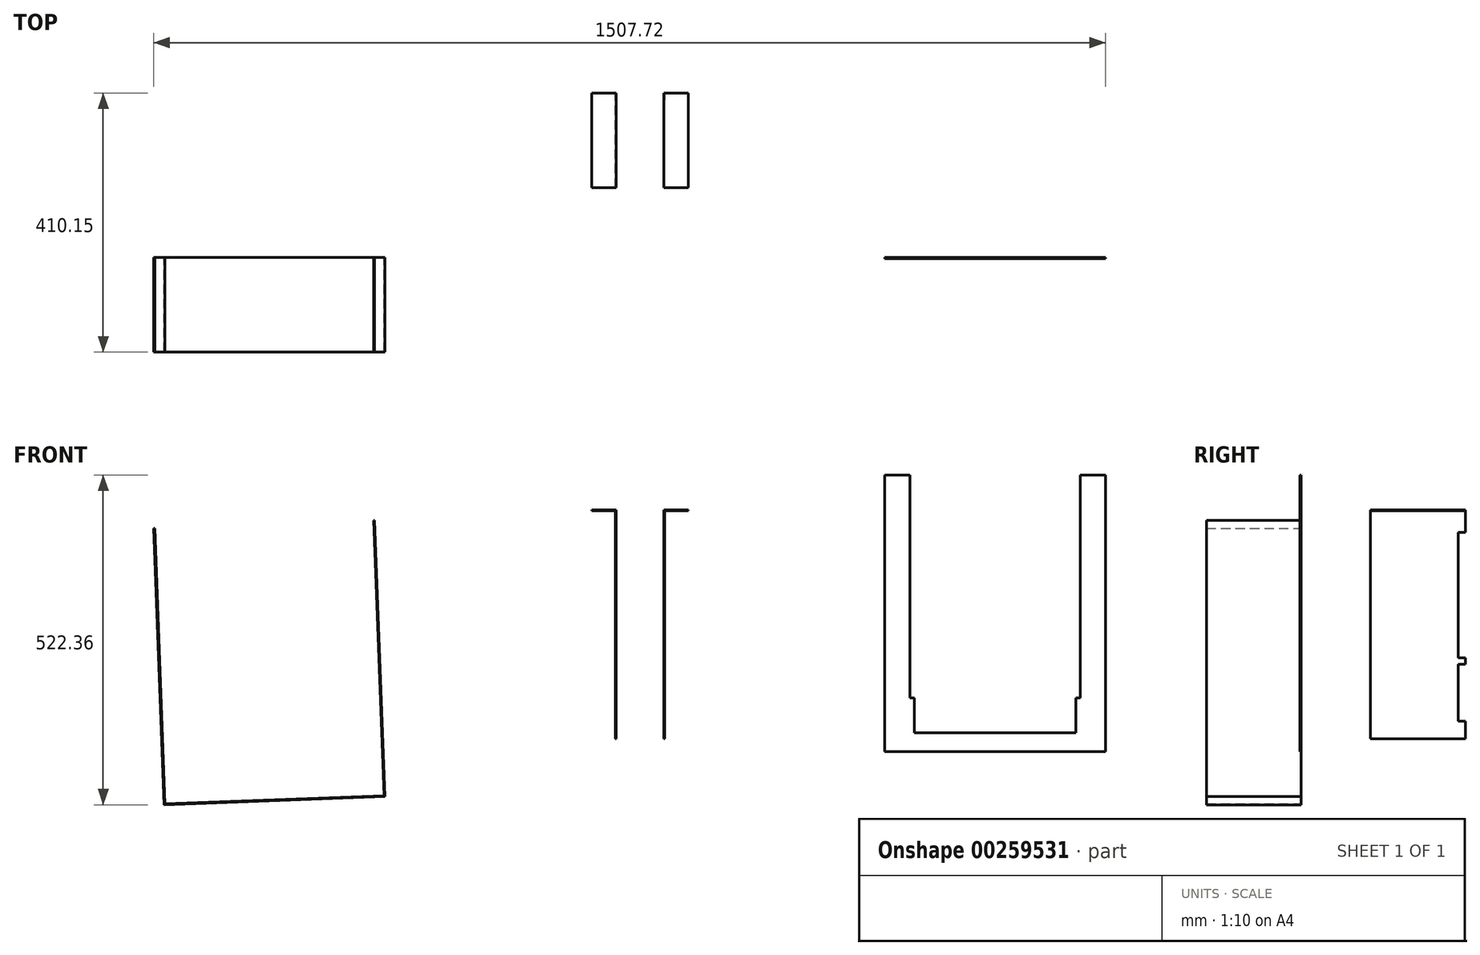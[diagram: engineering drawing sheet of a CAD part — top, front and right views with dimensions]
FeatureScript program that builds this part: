
annotation { "Feature Type Name" : "Feature", "Feature Type Description" : "" }
export const myFeature = defineFeature(function(context is Context, id is Id, definition is map)
    precondition{}
    {
        {
            var Q0;
            Q0=qCreatedBy(makeId("Front.planeOp"),FACE);
            var sketch = newSketch(context, id + "F0", { "sketchPlane" : qUnion([Q0])});
            skLineSegment(sketch, "E0", {"start": v(-308.3, 139.8) * mm, "end": v(-291.9, -297.9) * mm});
            skLineSegment(sketch, "E1", {"start": v(-291.9, -297.9) * mm, "end": v(-641.65, -311) * mm});
            skLineSegment(sketch, "E2", {"start": v(-641.65, -311) * mm, "end": v(-658.05, 126.7) * mm});
            skLineSegment(sketch, "E3", {"start": v(-658.05, 126.7) * mm, "end": v(-656.55, 126.75) * mm});
            skLineSegment(sketch, "E4", {"start": v(-656.55, 126.75) * mm, "end": v(-640.21, -309.44) * mm});
            skLineSegment(sketch, "E5", {"start": v(-640.21, -309.44) * mm, "end": v(-293.46, -296.45) * mm});
            skLineSegment(sketch, "E6", {"start": v(-293.46, -296.45) * mm, "end": v(-309.8, 139.74) * mm});
            skLineSegment(sketch, "E7", {"start": v(-309.8, 139.74) * mm, "end": v(-308.3, 139.8) * mm});
            skSolve(sketch);
        }
        {
            var Q0;
            Q0 = qSketchRegion(id + "F0", true);
            extrude(context, id + "F1", {"entities" : qUnion([Q0]), "depth" : 150 * mm});
        }
        {
            var Q0;
            Q0=qCreatedBy(makeId("Right.planeOp"),FACE);
            var sketch = newSketch(context, id + "F2", { "sketchPlane" : qUnion([Q0])});
            skLineSegment(sketch, "E8", {"start": v(148.65, 156.28) * mm, "end": v(110.15, 156.28) * mm});
            skLineSegment(sketch, "E9", {"start": v(110.15, 156.28) * mm, "end": v(110.15, -206.72) * mm});
            skLineSegment(sketch, "E10", {"start": v(110.15, -206.72) * mm, "end": v(111.65, -206.72) * mm});
            skLineSegment(sketch, "E11", {"start": v(111.65, -206.72) * mm, "end": v(111.65, 154.78) * mm});
            skLineSegment(sketch, "E12", {"start": v(111.65, 154.78) * mm, "end": v(148.65, 154.78) * mm});
            skLineSegment(sketch, "E13", {"start": v(148.65, 154.78) * mm, "end": v(148.65, 156.28) * mm});
            skSolve(sketch);
        }
        {
            var Q0;
            Q0=makeQuery(id+"F2.imprint","IMPRINT",FACE,{"disambiguationData":[TD([[makeQuery(id+"F2.imprint","IMPRINT",EDGE,{"derivedFrom":sQuery(id+"F2.wireOp",EDGE,"E8")}),1.0]])]});
            extrude(context, id + "F3", {"entities" : qUnion([Q0]), "depth" : 150 * mm});
        }
        {
            var Q0;
            Q0=makeQuery(id+"F3.opExtrude","SWEPT_FACE",FACE,{"disambiguationData":[OSD([sQuery(id+"F2.wireOp",EDGE,"E11")])]});
            var sketch = newSketch(context, id + "F4", { "sketchPlane" : qUnion([Q0])});
            skLineSegment(sketch, "E14", {"start": v(0, 120.28) * mm, "end": v(-11, 120.28) * mm});
            skLineSegment(sketch, "E15", {"start": v(-11, 120.28) * mm, "end": v(-11, -78.2) * mm});
            skLineSegment(sketch, "E16", {"start": v(-11, -78.2) * mm, "end": v(0, -78.2) * mm});
            skLineSegment(sketch, "E17", {"start": v(0, -88.2) * mm, "end": v(-11, -88.2) * mm});
            skLineSegment(sketch, "E18", {"start": v(-11, -88.2) * mm, "end": v(-11, -178.72) * mm});
            skLineSegment(sketch, "E19", {"start": v(-11, -178.72) * mm, "end": v(0, -178.72) * mm});
            skSolve(sketch);
        }
        {
            var Q0;
            {var subQ0=sQuery(id+"F4.wireOp",EDGE,"E14");Q0=makeQuery(id+"F4.imprint","IMPRINT",FACE,{"disambiguationData":[TD([[makeQuery(id+"F4.imprint","IMPRINT",EDGE,{"derivedFrom":subQ0}),1.0]])]});}
            var Q1;
            {var subQ0=sQuery(id+"F4.wireOp",EDGE,"E17");Q1=makeQuery(id+"F4.imprint","IMPRINT",FACE,{"disambiguationData":[TD([[makeQuery(id+"F4.imprint","IMPRINT",EDGE,{"derivedFrom":subQ0}),1.0]])]});}
            extrude(context, id + "F5", {"entities" : qUnion([Q0, Q1]), "operationType" : NewBodyOperationType.REMOVE, "oppositeDirection" : true, "depth" : 1.5 * mm});
        }
        {
            var Q0;
            Q0=makeQuery(id+"F3.opExtrude","SWEPT_BODY",BODY,{"disambiguationData":[OSD([sQuery(id+"F2.wireOp",EDGE,"E8"),sQuery(id+"F2.wireOp",EDGE,"E9"),sQuery(id+"F2.wireOp",EDGE,"E10"),sQuery(id+"F2.wireOp",EDGE,"E11"),sQuery(id+"F2.wireOp",EDGE,"E12"),sQuery(id+"F2.wireOp",EDGE,"E13")])]});
            var Q1;
            Q1=makeQuery(id+"F3.opExtrude","CAP_EDGE",EDGE,{"disambiguationData":[OSD([sQuery(id+"F2.wireOp",EDGE,"E9")])],"isStart":false});
            transform(context, id + "F6", {"entities" : qUnion([Q0]), "transformType" : TransformType.ROTATION, "transformAxis" : qUnion([Q1]), "angle" : 90 * degree, "makeCopy" : false});
        }
        {
            var Q0;
            Q0=makeQuery(id+"F3.opExtrude","SWEPT_BODY",BODY,{"disambiguationData":[OSD([sQuery(id+"F2.wireOp",EDGE,"E8"),sQuery(id+"F2.wireOp",EDGE,"E9"),sQuery(id+"F2.wireOp",EDGE,"E10"),sQuery(id+"F2.wireOp",EDGE,"E11"),sQuery(id+"F2.wireOp",EDGE,"E12"),sQuery(id+"F2.wireOp",EDGE,"E13")])]});
            var Q1;
            Q1=makeQuery(id+"F3.opExtrude","CAP_EDGE",EDGE,{"disambiguationData":[OSD([sQuery(id+"F2.wireOp",EDGE,"E12")])],"isStart":true});
            transform(context, id + "F7", {"entities" : qUnion([Q0]), "transformType" : TransformType.TRANSLATION_ENTITY, "oppositeDirectionEntity" : true, "transformLine" : qUnion([Q1]), "makeCopy" : true});
        }
        {
            var Q0;
            Q0=makeQuery(id+"F7.opPattern","COPY",BODY,{"derivedFrom":makeQuery(id+"F3.opExtrude","SWEPT_BODY",BODY,{"disambiguationData":[OSD([sQuery(id+"F2.wireOp",EDGE,"E8"),sQuery(id+"F2.wireOp",EDGE,"E9"),sQuery(id+"F2.wireOp",EDGE,"E10"),sQuery(id+"F2.wireOp",EDGE,"E11"),sQuery(id+"F2.wireOp",EDGE,"E12"),sQuery(id+"F2.wireOp",EDGE,"E13")])]}),"instanceName":"1"});
            var Q1;
            Q1=makeQuery(id+"F7.opPattern","COPY",EDGE,{"derivedFrom":makeQuery(id+"F3.opExtrude","CAP_EDGE",EDGE,{"disambiguationData":[OSD([sQuery(id+"F2.wireOp",EDGE,"E8")])],"isStart":true}),"instanceName":"1"});
            transform(context, id + "F8", {"entities" : qUnion([Q0]), "transformType" : TransformType.TRANSLATION_ENTITY, "oppositeDirectionEntity" : false, "transformLine" : qUnion([Q1]), "makeCopy" : false});
        }
        {
            var Q0;
            Q0=qCreatedBy(makeId("Front.planeOp"),FACE);
            var sketch = newSketch(context, id + "F9", { "sketchPlane" : qUnion([Q0])});
            skLineSegment(sketch, "E20", {"start": v(849.67, 211.36) * mm, "end": v(849.67, -226.64) * mm});
            skLineSegment(sketch, "E21", {"start": v(849.67, -226.64) * mm, "end": v(499.67, -226.64) * mm});
            skLineSegment(sketch, "E22", {"start": v(499.67, -226.64) * mm, "end": v(499.67, 211.36) * mm});
            skLineSegment(sketch, "E23", {"start": v(499.67, 211.36) * mm, "end": v(539.67, 211.36) * mm});
            skLineSegment(sketch, "E24", {"start": v(539.67, 211.36) * mm, "end": v(539.67, -141.64) * mm});
            skLineSegment(sketch, "E25", {"start": v(539.67, -141.64) * mm, "end": v(546.67, -141.64) * mm});
            skLineSegment(sketch, "E26", {"start": v(546.67, -141.64) * mm, "end": v(546.67, -196.64) * mm});
            skLineSegment(sketch, "E27", {"start": v(546.67, -196.64) * mm, "end": v(802.67, -196.64) * mm});
            skLineSegment(sketch, "E28", {"start": v(802.67, -196.64) * mm, "end": v(802.67, -141.64) * mm});
            skLineSegment(sketch, "E29", {"start": v(802.67, -141.64) * mm, "end": v(809.67, -141.64) * mm});
            skLineSegment(sketch, "E30", {"start": v(809.67, -141.64) * mm, "end": v(809.67, 211.36) * mm});
            skLineSegment(sketch, "E31", {"start": v(809.67, 211.36) * mm, "end": v(849.67, 211.36) * mm});
            skSolve(sketch);
        }
        {
            var Q0;
            Q0=makeQuery(id+"F9.imprint","IMPRINT",FACE,{"disambiguationData":[TD([[makeQuery(id+"F9.imprint","IMPRINT",EDGE,{"derivedFrom":sQuery(id+"F9.wireOp",EDGE,"E20")}),-1.0]])]});
            extrude(context, id + "F10", {"entities" : qUnion([Q0]), "depth" : 2 * mm});
        }
        {
            var Q0;
            Q0=makeQuery(id+"F7.opPattern","COPY",BODY,{"derivedFrom":makeQuery(id+"F3.opExtrude","SWEPT_BODY",BODY,{"disambiguationData":[OSD([sQuery(id+"F2.wireOp",EDGE,"E8"),sQuery(id+"F2.wireOp",EDGE,"E9"),sQuery(id+"F2.wireOp",EDGE,"E10"),sQuery(id+"F2.wireOp",EDGE,"E11"),sQuery(id+"F2.wireOp",EDGE,"E12"),sQuery(id+"F2.wireOp",EDGE,"E13")])]}),"instanceName":"1"});
            var Q1;
            Q1=makeQuery(id+"F7.opPattern","COPY",FACE,{"derivedFrom":makeQuery(id+"F3.opExtrude","SWEPT_FACE",FACE,{"disambiguationData":[OSD([sQuery(id+"F2.wireOp",EDGE,"E9")])]}),"instanceName":"1"});
            mirror(context, id + "F11", {"entities" : qUnion([Q0]), "mirrorPlane" : qUnion([Q1])});
        }
        {
            var Q0;
            Q0=makeQuery(id+"F7.opPattern","COPY",BODY,{"derivedFrom":makeQuery(id+"F3.opExtrude","SWEPT_BODY",BODY,{"disambiguationData":[OSD([sQuery(id+"F2.wireOp",EDGE,"E8"),sQuery(id+"F2.wireOp",EDGE,"E9"),sQuery(id+"F2.wireOp",EDGE,"E10"),sQuery(id+"F2.wireOp",EDGE,"E11"),sQuery(id+"F2.wireOp",EDGE,"E12"),sQuery(id+"F2.wireOp",EDGE,"E13")])]}),"instanceName":"1"});
            deleteBodies(context, id + "F12", {"entities" : qUnion([Q0])});
        }
    });
